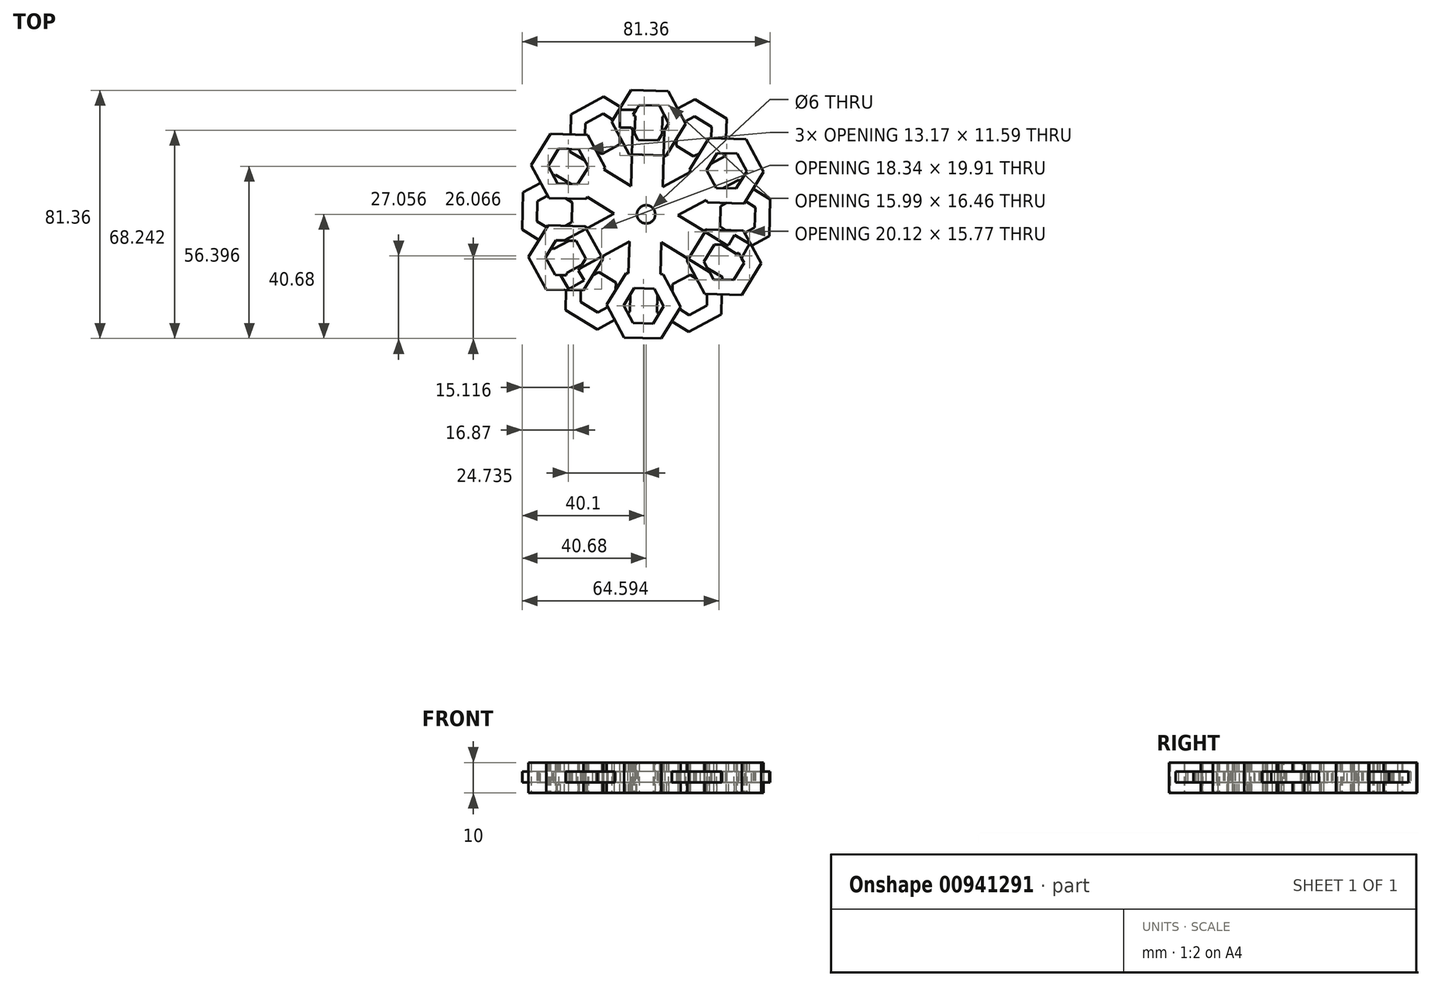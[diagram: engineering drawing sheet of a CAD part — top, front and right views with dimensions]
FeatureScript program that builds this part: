
annotation { "Feature Type Name" : "Feature", "Feature Type Description" : "" }
export const myFeature = defineFeature(function(context is Context, id is Id, definition is map)
    precondition{}
    {
        {
            var Q0;
            Q0=qCreatedBy(makeId("Top.planeOp"),FACE);
            var sketch = newSketch(context, id + "F0", { "sketchPlane" : qUnion([Q0])});
            skCircle(sketch, "E0", {"center": v(0, 0) * mm, "radius": 3 * mm});
            skSolve(sketch);
        }
        {
            var Q0;
            Q0=qCreatedBy(makeId("Top.planeOp"),FACE);
            var sketch = newSketch(context, id + "F1", { "sketchPlane" : qUnion([Q0])});
            skPoint(sketch, "E1.0.midPoint", {"position": v(0, 0) * mm});
            skCircle(sketch, "E2.cCircle", {"center": v(0, 0) * mm, "radius": 9.08 * mm, "construction": true});
            skLineSegment(sketch, "E2.0", {"start": v(-8.93, 5.5) * mm, "end": v(0.29, 10.48) * mm});
            skLineSegment(sketch, "E2.1", {"start": v(0.29, 10.48) * mm, "end": v(9.22, 5) * mm});
            skLineSegment(sketch, "E2.2", {"start": v(9.22, 5) * mm, "end": v(8.93, -5.5) * mm});
            skLineSegment(sketch, "E2.3", {"start": v(8.93, -5.5) * mm, "end": v(-0.29, -10.48) * mm});
            skLineSegment(sketch, "E2.4", {"start": v(-0.29, -10.48) * mm, "end": v(-9.22, -5) * mm});
            skLineSegment(sketch, "E2.5", {"start": v(-9.22, -5) * mm, "end": v(-8.93, 5.5) * mm});
            skPoint(sketch, "E2.0.midPoint", {"position": v(-4.32, 7.99) * mm});
            skLineSegment(sketch, "E3", {"start": v(-9.22, -5) * mm, "end": v(-30, -4.42) * mm});
            skLineSegment(sketch, "E4", {"start": v(-8.93, 5.5) * mm, "end": v(-30, 6.07) * mm});
            skLineSegment(sketch, "E5", {"start": v(-30, 6.07) * mm, "end": v(-30, -4.42) * mm});
            skCircle(sketch, "E6.cCircle", {"center": v(-30, 0.83) * mm, "radius": 10.52 * mm, "construction": true});
            skLineSegment(sketch, "E6.0", {"start": v(-40.68, -4.95) * mm, "end": v(-40.35, 7.2) * mm});
            skLineSegment(sketch, "E6.1", {"start": v(-40.35, 7.2) * mm, "end": v(-29.66, 12.98) * mm});
            skLineSegment(sketch, "E6.2", {"start": v(-29.66, 12.98) * mm, "end": v(-19.3, 6.61) * mm});
            skLineSegment(sketch, "E6.3", {"start": v(-19.3, 6.61) * mm, "end": v(-19.64, -5.54) * mm});
            skLineSegment(sketch, "E6.4", {"start": v(-19.64, -5.54) * mm, "end": v(-30.33, -11.32) * mm});
            skLineSegment(sketch, "E6.5", {"start": v(-30.33, -11.32) * mm, "end": v(-40.68, -4.95) * mm});
            skPoint(sketch, "E6.0.midPoint", {"position": v(-40.52, 1.12) * mm});
            skLineSegment(sketch, "E7.0", {"start": v(-35.8, -2.3) * mm, "end": v(-35.6, 4.28) * mm});
            skLineSegment(sketch, "E7.1", {"start": v(-35.6, 4.28) * mm, "end": v(-29.81, 7.41) * mm});
            skLineSegment(sketch, "E7.2", {"start": v(-29.81, 7.41) * mm, "end": v(-24.2, 3.96) * mm});
            skLineSegment(sketch, "E7.3", {"start": v(-24.2, 3.96) * mm, "end": v(-24.38, -2.62) * mm});
            skLineSegment(sketch, "E7.4", {"start": v(-24.38, -2.62) * mm, "end": v(-30.18, -5.76) * mm});
            skLineSegment(sketch, "E7.5", {"start": v(-30.18, -5.76) * mm, "end": v(-35.8, -2.3) * mm});
            skPoint(sketch, "E7.0.midPoint", {"position": v(-35.7, 0.99) * mm});
            skLineSegment(sketch, "E8.1.1", {"start": v(-15.38, -13.42) * mm, "end": v(-5.03, -19.78) * mm});
            skLineSegment(sketch, "E8.1.2", {"start": v(-5.36, -31.93) * mm, "end": v(-16.05, -37.71) * mm});
            skLineSegment(sketch, "E8.1.3", {"start": v(-16.05, -37.71) * mm, "end": v(-26.4, -31.35) * mm});
            skLineSegment(sketch, "E8.1.4", {"start": v(-26.4, -31.35) * mm, "end": v(-26.07, -19.2) * mm});
            skLineSegment(sketch, "E8.1.5", {"start": v(-26.07, -19.2) * mm, "end": v(-15.38, -13.42) * mm});
            skCircle(sketch, "E8.1.6", {"center": v(-15.72, -25.56) * mm, "radius": 9.53 * mm, "construction": true});
            skCircle(sketch, "E8.1.7", {"center": v(-15.72, -25.56) * mm, "radius": 10.52 * mm, "construction": true});
            skLineSegment(sketch, "E8.1.8", {"start": v(-5.03, -19.78) * mm, "end": v(-5.36, -31.93) * mm});
            skLineSegment(sketch, "E8.1.9", {"start": v(-9.22, -5) * mm, "end": v(-20.26, -22.94) * mm});
            skLineSegment(sketch, "E8.1.10", {"start": v(-0.29, -10.48) * mm, "end": v(-11.17, -28.19) * mm});
            skLineSegment(sketch, "E8.1.11", {"start": v(-20.26, -22.94) * mm, "end": v(-11.17, -28.19) * mm});
            skLineSegment(sketch, "E8.2.1", {"start": v(3.93, -20.03) * mm, "end": v(14.62, -14.24) * mm});
            skLineSegment(sketch, "E8.2.2", {"start": v(24.97, -20.6) * mm, "end": v(24.63, -32.76) * mm});
            skLineSegment(sketch, "E8.2.3", {"start": v(24.63, -32.76) * mm, "end": v(13.95, -38.54) * mm});
            skLineSegment(sketch, "E8.2.4", {"start": v(13.95, -38.54) * mm, "end": v(3.6, -32.18) * mm});
            skLineSegment(sketch, "E8.2.5", {"start": v(3.6, -32.18) * mm, "end": v(3.93, -20.03) * mm});
            skCircle(sketch, "E8.2.6", {"center": v(14.28, -26.4) * mm, "radius": 9.53 * mm, "construction": true});
            skCircle(sketch, "E8.2.7", {"center": v(14.28, -26.4) * mm, "radius": 10.52 * mm, "construction": true});
            skLineSegment(sketch, "E8.2.8", {"start": v(14.62, -14.24) * mm, "end": v(24.97, -20.6) * mm});
            skLineSegment(sketch, "E8.2.9", {"start": v(-0.29, -10.48) * mm, "end": v(9.74, -29.01) * mm});
            skLineSegment(sketch, "E8.2.10", {"start": v(8.93, -5.5) * mm, "end": v(18.82, -23.77) * mm});
            skLineSegment(sketch, "E8.2.11", {"start": v(9.74, -29.01) * mm, "end": v(18.82, -23.77) * mm});
            skLineSegment(sketch, "E8.3.1", {"start": v(19.3, -6.61) * mm, "end": v(19.64, 5.54) * mm});
            skLineSegment(sketch, "E8.3.2", {"start": v(30.33, 11.32) * mm, "end": v(40.68, 4.95) * mm});
            skLineSegment(sketch, "E8.3.3", {"start": v(40.68, 4.95) * mm, "end": v(40.35, -7.2) * mm});
            skLineSegment(sketch, "E8.3.4", {"start": v(40.35, -7.2) * mm, "end": v(29.66, -12.98) * mm});
            skLineSegment(sketch, "E8.3.5", {"start": v(29.66, -12.98) * mm, "end": v(19.3, -6.61) * mm});
            skCircle(sketch, "E8.3.6", {"center": v(30, -0.83) * mm, "radius": 9.53 * mm, "construction": true});
            skCircle(sketch, "E8.3.7", {"center": v(30, -0.83) * mm, "radius": 10.52 * mm, "construction": true});
            skLineSegment(sketch, "E8.3.8", {"start": v(19.64, 5.54) * mm, "end": v(30.33, 11.32) * mm});
            skLineSegment(sketch, "E8.3.9", {"start": v(8.93, -5.5) * mm, "end": v(30, -6.07) * mm});
            skLineSegment(sketch, "E8.3.10", {"start": v(9.22, 5) * mm, "end": v(30, 4.42) * mm});
            skLineSegment(sketch, "E8.3.11", {"start": v(30, -6.07) * mm, "end": v(30, 4.42) * mm});
            skLineSegment(sketch, "E8.4.1", {"start": v(15.38, 13.42) * mm, "end": v(5.03, 19.78) * mm});
            skLineSegment(sketch, "E8.4.2", {"start": v(5.36, 31.93) * mm, "end": v(16.05, 37.71) * mm});
            skLineSegment(sketch, "E8.4.3", {"start": v(16.05, 37.71) * mm, "end": v(26.4, 31.35) * mm});
            skLineSegment(sketch, "E8.4.4", {"start": v(26.4, 31.35) * mm, "end": v(26.07, 19.2) * mm});
            skLineSegment(sketch, "E8.4.5", {"start": v(26.07, 19.2) * mm, "end": v(15.38, 13.42) * mm});
            skCircle(sketch, "E8.4.6", {"center": v(15.72, 25.56) * mm, "radius": 9.53 * mm, "construction": true});
            skCircle(sketch, "E8.4.7", {"center": v(15.72, 25.56) * mm, "radius": 10.52 * mm, "construction": true});
            skLineSegment(sketch, "E8.4.8", {"start": v(5.03, 19.78) * mm, "end": v(5.36, 31.93) * mm});
            skLineSegment(sketch, "E8.4.9", {"start": v(9.22, 5) * mm, "end": v(20.26, 22.94) * mm});
            skLineSegment(sketch, "E8.4.10", {"start": v(0.29, 10.48) * mm, "end": v(11.17, 28.19) * mm});
            skLineSegment(sketch, "E8.4.11", {"start": v(20.26, 22.94) * mm, "end": v(11.17, 28.19) * mm});
            skLineSegment(sketch, "E8.5.1", {"start": v(-3.93, 20.03) * mm, "end": v(-14.62, 14.24) * mm});
            skLineSegment(sketch, "E8.5.2", {"start": v(-24.97, 20.6) * mm, "end": v(-24.63, 32.76) * mm});
            skLineSegment(sketch, "E8.5.3", {"start": v(-24.63, 32.76) * mm, "end": v(-13.95, 38.54) * mm});
            skLineSegment(sketch, "E8.5.4", {"start": v(-13.95, 38.54) * mm, "end": v(-3.6, 32.18) * mm});
            skLineSegment(sketch, "E8.5.5", {"start": v(-3.6, 32.18) * mm, "end": v(-3.93, 20.03) * mm});
            skCircle(sketch, "E8.5.6", {"center": v(-14.28, 26.4) * mm, "radius": 9.53 * mm, "construction": true});
            skCircle(sketch, "E8.5.7", {"center": v(-14.28, 26.4) * mm, "radius": 10.52 * mm, "construction": true});
            skLineSegment(sketch, "E8.5.8", {"start": v(-14.62, 14.24) * mm, "end": v(-24.97, 20.6) * mm});
            skLineSegment(sketch, "E8.5.9", {"start": v(0.29, 10.48) * mm, "end": v(-9.74, 29.01) * mm});
            skLineSegment(sketch, "E8.5.10", {"start": v(-8.93, 5.5) * mm, "end": v(-18.82, 23.77) * mm});
            skLineSegment(sketch, "E8.5.11", {"start": v(-9.74, 29.01) * mm, "end": v(-18.82, 23.77) * mm});
            skLineSegment(sketch, "E9.1.1", {"start": v(8.67, -22.94) * mm, "end": v(14.46, -19.8) * mm});
            skPoint(sketch, "E9.1.2", {"position": v(17, -31.41) * mm});
            skCircle(sketch, "E9.1.3", {"center": v(14.28, -26.4) * mm, "radius": 5.7 * mm, "construction": true});
            skLineSegment(sketch, "E9.2.1", {"start": v(15.53, 18.98) * mm, "end": v(9.92, 22.43) * mm});
            skPoint(sketch, "E9.2.2", {"position": v(18.7, 30.42) * mm});
            skCircle(sketch, "E9.2.3", {"center": v(15.72, 25.56) * mm, "radius": 5.7 * mm, "construction": true});
            skLineSegment(sketch, "E10.1.1", {"start": v(-15.53, -18.98) * mm, "end": v(-9.92, -22.43) * mm});
            skLineSegment(sketch, "E10.1.2", {"start": v(-9.92, -22.43) * mm, "end": v(-10.1, -29.01) * mm});
            skLineSegment(sketch, "E10.1.3", {"start": v(-10.1, -29.01) * mm, "end": v(-15.9, -32.15) * mm});
            skLineSegment(sketch, "E10.1.4", {"start": v(-15.9, -32.15) * mm, "end": v(-21.51, -28.7) * mm});
            skLineSegment(sketch, "E10.1.5", {"start": v(-21.51, -28.7) * mm, "end": v(-21.33, -22.11) * mm});
            skLineSegment(sketch, "E10.1.6", {"start": v(-21.33, -22.11) * mm, "end": v(-15.53, -18.98) * mm});
            skLineSegment(sketch, "E10.2.2", {"start": v(14.46, -19.8) * mm, "end": v(20.08, -23.26) * mm});
            skLineSegment(sketch, "E10.2.3", {"start": v(20.08, -23.26) * mm, "end": v(19.9, -29.84) * mm});
            skLineSegment(sketch, "E10.2.4", {"start": v(19.9, -29.84) * mm, "end": v(14.1, -32.98) * mm});
            skLineSegment(sketch, "E10.2.5", {"start": v(14.1, -32.98) * mm, "end": v(8.49, -29.53) * mm});
            skLineSegment(sketch, "E10.2.6", {"start": v(8.49, -29.53) * mm, "end": v(8.67, -22.94) * mm});
            skLineSegment(sketch, "E10.3.1", {"start": v(24.2, -3.96) * mm, "end": v(24.38, 2.62) * mm});
            skLineSegment(sketch, "E10.3.2", {"start": v(24.38, 2.62) * mm, "end": v(30.18, 5.76) * mm});
            skLineSegment(sketch, "E10.3.3", {"start": v(30.18, 5.76) * mm, "end": v(35.8, 2.3) * mm});
            skLineSegment(sketch, "E10.3.4", {"start": v(35.8, 2.3) * mm, "end": v(35.6, -4.28) * mm});
            skLineSegment(sketch, "E10.3.5", {"start": v(35.6, -4.28) * mm, "end": v(29.81, -7.41) * mm});
            skLineSegment(sketch, "E10.3.6", {"start": v(29.81, -7.41) * mm, "end": v(24.2, -3.96) * mm});
            skLineSegment(sketch, "E10.4.2", {"start": v(9.92, 22.43) * mm, "end": v(10.1, 29.01) * mm});
            skLineSegment(sketch, "E10.4.3", {"start": v(10.1, 29.01) * mm, "end": v(15.9, 32.15) * mm});
            skLineSegment(sketch, "E10.4.4", {"start": v(15.9, 32.15) * mm, "end": v(21.51, 28.7) * mm});
            skLineSegment(sketch, "E10.4.5", {"start": v(21.51, 28.7) * mm, "end": v(21.33, 22.11) * mm});
            skLineSegment(sketch, "E10.4.6", {"start": v(21.33, 22.11) * mm, "end": v(15.53, 18.98) * mm});
            skLineSegment(sketch, "E10.5.1", {"start": v(-8.67, 22.94) * mm, "end": v(-14.46, 19.8) * mm});
            skLineSegment(sketch, "E10.5.2", {"start": v(-14.46, 19.8) * mm, "end": v(-20.08, 23.26) * mm});
            skLineSegment(sketch, "E10.5.3", {"start": v(-20.08, 23.26) * mm, "end": v(-19.9, 29.84) * mm});
            skLineSegment(sketch, "E10.5.4", {"start": v(-19.9, 29.84) * mm, "end": v(-14.1, 32.98) * mm});
            skLineSegment(sketch, "E10.5.5", {"start": v(-14.1, 32.98) * mm, "end": v(-8.49, 29.53) * mm});
            skLineSegment(sketch, "E10.5.6", {"start": v(-8.49, 29.53) * mm, "end": v(-8.67, 22.94) * mm});
            skLineSegment(sketch, "E11", {"start": v(-15.38, -13.42) * mm, "end": v(-7.57, -13.42) * mm});
            skLineSegment(sketch, "E12", {"start": v(-7.57, -13.42) * mm, "end": v(-5.03, -19.78) * mm});
            skLineSegment(sketch, "E13.1.1", {"start": v(15.4, 0.15) * mm, "end": v(19.64, 5.54) * mm});
            skLineSegment(sketch, "E13.1.3", {"start": v(19.3, -6.61) * mm, "end": v(15.4, 0.15) * mm});
            skLineSegment(sketch, "E13.2.1", {"start": v(-7.83, 13.27) * mm, "end": v(-14.62, 14.24) * mm});
            skLineSegment(sketch, "E13.2.3", {"start": v(-3.93, 20.03) * mm, "end": v(-7.83, 13.27) * mm});
            skLineSegment(sketch, "E14.bottom", {"start": v(28.48, 8.57) * mm, "end": v(34.28, 8.57) * mm});
            skLineSegment(sketch, "E14.top", {"start": v(28.48, -10.48) * mm, "end": v(34.28, -10.48) * mm});
            skLineSegment(sketch, "E14.left", {"start": v(28.48, 8.57) * mm, "end": v(28.48, -10.48) * mm});
            skLineSegment(sketch, "E14.right", {"start": v(34.28, 8.57) * mm, "end": v(34.28, -10.48) * mm});
            skLineSegment(sketch, "E15.1.1", {"start": v(-21.66, 20.37) * mm, "end": v(-5.17, 29.9) * mm});
            skLineSegment(sketch, "E15.1.2", {"start": v(-21.66, 20.37) * mm, "end": v(-24.57, 25.4) * mm});
            skLineSegment(sketch, "E15.1.3", {"start": v(-24.57, 25.4) * mm, "end": v(-8.07, 34.93) * mm});
            skLineSegment(sketch, "E15.1.4", {"start": v(-5.17, 29.9) * mm, "end": v(-8.07, 34.93) * mm});
            skLineSegment(sketch, "E15.2.1", {"start": v(-6.81, -28.95) * mm, "end": v(-23.31, -19.42) * mm});
            skLineSegment(sketch, "E15.2.2", {"start": v(-6.81, -28.95) * mm, "end": v(-9.71, -33.98) * mm});
            skLineSegment(sketch, "E15.2.3", {"start": v(-9.71, -33.98) * mm, "end": v(-26.21, -24.45) * mm});
            skLineSegment(sketch, "E15.2.4", {"start": v(-23.31, -19.42) * mm, "end": v(-26.21, -24.45) * mm});
            skSolve(sketch);
        }
        {
            var Q0;
            Q0 = qSketchRegion(id + "F1", true);
            extrude(context, id + "F2", {"entities" : qUnion([Q0]), "depth" : 3.5 * mm, "offsetDistance" : 25.4 * mm});
        }
        {
            var Q0;
            Q0=makeQuery(id+"F0.imprint","IMPRINT",FACE,{"disambiguationData":[TD([[makeQuery(id+"F0.imprint","IMPRINT",EDGE,{"derivedFrom":sQuery(id+"F0.wireOp",EDGE,"E0")}),1.0]])]});
            extrude(context, id + "F3", {"entities" : qUnion([Q0]), "operationType" : NewBodyOperationType.REMOVE, "oppositeDirection" : true, "depth" : 25.4 * mm, "offsetDistance" : 25.4 * mm, "hasSecondDirection" : true, "secondDirectionOppositeDirection" : false, "secondDirectionDepth" : 25.4 * mm});
        }
        {
            var Q0;
            Q0=makeQuery(id+"F2.opExtrude","SWEPT_BODY",BODY,{"disambiguationData":[OSD([sQuery(id+"F1.wireOp",EDGE,"E3"),sQuery(id+"F1.wireOp",EDGE,"E4"),sQuery(id+"F1.wireOp",EDGE,"E6.0"),sQuery(id+"F1.wireOp",EDGE,"E6.1"),sQuery(id+"F1.wireOp",EDGE,"E6.2"),sQuery(id+"F1.wireOp",EDGE,"E6.3"),sQuery(id+"F1.wireOp",EDGE,"E6.4"),sQuery(id+"F1.wireOp",EDGE,"E6.5"),sQuery(id+"F1.wireOp",EDGE,"E7.0"),sQuery(id+"F1.wireOp",EDGE,"E7.1"),sQuery(id+"F1.wireOp",EDGE,"E7.2"),sQuery(id+"F1.wireOp",EDGE,"E7.3"),sQuery(id+"F1.wireOp",EDGE,"E7.4"),sQuery(id+"F1.wireOp",EDGE,"E7.5"),sQuery(id+"F1.wireOp",EDGE,"E8.1.1"),sQuery(id+"F1.wireOp",EDGE,"E8.1.2"),sQuery(id+"F1.wireOp",EDGE,"E8.1.3"),sQuery(id+"F1.wireOp",EDGE,"E8.1.4"),sQuery(id+"F1.wireOp",EDGE,"E8.1.5"),sQuery(id+"F1.wireOp",EDGE,"E8.1.8"),sQuery(id+"F1.wireOp",EDGE,"E8.1.9"),sQuery(id+"F1.wireOp",EDGE,"E8.1.10"),sQuery(id+"F1.wireOp",EDGE,"E8.2.1"),sQuery(id+"F1.wireOp",EDGE,"E8.2.2"),sQuery(id+"F1.wireOp",EDGE,"E8.2.3"),sQuery(id+"F1.wireOp",EDGE,"E8.2.4"),sQuery(id+"F1.wireOp",EDGE,"E8.2.5"),sQuery(id+"F1.wireOp",EDGE,"E8.2.8"),sQuery(id+"F1.wireOp",EDGE,"E8.2.9"),sQuery(id+"F1.wireOp",EDGE,"E8.2.10"),sQuery(id+"F1.wireOp",EDGE,"E8.3.1"),sQuery(id+"F1.wireOp",EDGE,"E8.3.2"),sQuery(id+"F1.wireOp",EDGE,"E8.3.3"),sQuery(id+"F1.wireOp",EDGE,"E8.3.4"),sQuery(id+"F1.wireOp",EDGE,"E8.3.5"),sQuery(id+"F1.wireOp",EDGE,"E8.3.8"),sQuery(id+"F1.wireOp",EDGE,"E8.3.9"),sQuery(id+"F1.wireOp",EDGE,"E8.3.10"),sQuery(id+"F1.wireOp",EDGE,"E8.4.1"),sQuery(id+"F1.wireOp",EDGE,"E8.4.2"),sQuery(id+"F1.wireOp",EDGE,"E8.4.3"),sQuery(id+"F1.wireOp",EDGE,"E8.4.4"),sQuery(id+"F1.wireOp",EDGE,"E8.4.5"),sQuery(id+"F1.wireOp",EDGE,"E8.4.8"),sQuery(id+"F1.wireOp",EDGE,"E8.4.9"),sQuery(id+"F1.wireOp",EDGE,"E8.4.10"),sQuery(id+"F1.wireOp",EDGE,"E8.5.1"),sQuery(id+"F1.wireOp",EDGE,"E8.5.2"),sQuery(id+"F1.wireOp",EDGE,"E8.5.3"),sQuery(id+"F1.wireOp",EDGE,"E8.5.4"),sQuery(id+"F1.wireOp",EDGE,"E8.5.5"),sQuery(id+"F1.wireOp",EDGE,"E8.5.8"),sQuery(id+"F1.wireOp",EDGE,"E8.5.9"),sQuery(id+"F1.wireOp",EDGE,"E8.5.10")])]});
            var Q1;
            Q1=makeQuery(id+"F3.boolean.opBoolean","INTERSECT",EDGE,{"derivedFrom":[makeQuery(id+"F2.opExtrude","CAP_FACE",FACE,{"disambiguationData":[OSD([sQuery(id+"F1.wireOp",EDGE,"E3"),sQuery(id+"F1.wireOp",EDGE,"E4"),sQuery(id+"F1.wireOp",EDGE,"E6.0"),sQuery(id+"F1.wireOp",EDGE,"E6.1"),sQuery(id+"F1.wireOp",EDGE,"E6.2"),sQuery(id+"F1.wireOp",EDGE,"E6.3"),sQuery(id+"F1.wireOp",EDGE,"E6.4"),sQuery(id+"F1.wireOp",EDGE,"E6.5"),sQuery(id+"F1.wireOp",EDGE,"E7.0"),sQuery(id+"F1.wireOp",EDGE,"E7.1"),sQuery(id+"F1.wireOp",EDGE,"E7.2"),sQuery(id+"F1.wireOp",EDGE,"E7.3"),sQuery(id+"F1.wireOp",EDGE,"E7.4"),sQuery(id+"F1.wireOp",EDGE,"E7.5"),sQuery(id+"F1.wireOp",EDGE,"E8.1.1"),sQuery(id+"F1.wireOp",EDGE,"E8.1.2"),sQuery(id+"F1.wireOp",EDGE,"E8.1.3"),sQuery(id+"F1.wireOp",EDGE,"E8.1.4"),sQuery(id+"F1.wireOp",EDGE,"E8.1.5"),sQuery(id+"F1.wireOp",EDGE,"E8.1.8"),sQuery(id+"F1.wireOp",EDGE,"E8.1.9"),sQuery(id+"F1.wireOp",EDGE,"E8.1.10"),sQuery(id+"F1.wireOp",EDGE,"E8.2.1"),sQuery(id+"F1.wireOp",EDGE,"E8.2.2"),sQuery(id+"F1.wireOp",EDGE,"E8.2.3"),sQuery(id+"F1.wireOp",EDGE,"E8.2.4"),sQuery(id+"F1.wireOp",EDGE,"E8.2.5"),sQuery(id+"F1.wireOp",EDGE,"E8.2.8"),sQuery(id+"F1.wireOp",EDGE,"E8.2.9"),sQuery(id+"F1.wireOp",EDGE,"E8.2.10"),sQuery(id+"F1.wireOp",EDGE,"E8.3.1"),sQuery(id+"F1.wireOp",EDGE,"E8.3.2"),sQuery(id+"F1.wireOp",EDGE,"E8.3.3"),sQuery(id+"F1.wireOp",EDGE,"E8.3.4"),sQuery(id+"F1.wireOp",EDGE,"E8.3.5"),sQuery(id+"F1.wireOp",EDGE,"E8.3.8"),sQuery(id+"F1.wireOp",EDGE,"E8.3.9"),sQuery(id+"F1.wireOp",EDGE,"E8.3.10"),sQuery(id+"F1.wireOp",EDGE,"E8.4.1"),sQuery(id+"F1.wireOp",EDGE,"E8.4.2"),sQuery(id+"F1.wireOp",EDGE,"E8.4.3"),sQuery(id+"F1.wireOp",EDGE,"E8.4.4"),sQuery(id+"F1.wireOp",EDGE,"E8.4.5"),sQuery(id+"F1.wireOp",EDGE,"E8.4.8"),sQuery(id+"F1.wireOp",EDGE,"E8.4.9"),sQuery(id+"F1.wireOp",EDGE,"E8.4.10"),sQuery(id+"F1.wireOp",EDGE,"E8.5.1"),sQuery(id+"F1.wireOp",EDGE,"E8.5.2"),sQuery(id+"F1.wireOp",EDGE,"E8.5.3"),sQuery(id+"F1.wireOp",EDGE,"E8.5.4"),sQuery(id+"F1.wireOp",EDGE,"E8.5.5"),sQuery(id+"F1.wireOp",EDGE,"E8.5.8"),sQuery(id+"F1.wireOp",EDGE,"E8.5.9"),sQuery(id+"F1.wireOp",EDGE,"E8.5.10")])],"isStart":false}),makeQuery(id+"F3.opExtrude","SWEPT_FACE",FACE,{"disambiguationData":[OSD([sQuery(id+"F0.wireOp",EDGE,"E0")])]})]});
            circularPattern(context, id + "F4", {"entities" : qUnion([Q0]), "axis" : qUnion([Q1]), "angle" : 360 * degree, "instanceCount" : 4, "equalSpace" : true});
        }
        {
            var Q0;
            Q0=makeQuery(id+"F4.opPattern","COPY",FACE,{"derivedFrom":makeQuery(id+"F2.opExtrude","CAP_FACE",FACE,{"disambiguationData":[OSD([sQuery(id+"F1.wireOp",EDGE,"E3"),sQuery(id+"F1.wireOp",EDGE,"E4"),sQuery(id+"F1.wireOp",EDGE,"E6.0"),sQuery(id+"F1.wireOp",EDGE,"E6.1"),sQuery(id+"F1.wireOp",EDGE,"E6.2"),sQuery(id+"F1.wireOp",EDGE,"E6.3"),sQuery(id+"F1.wireOp",EDGE,"E6.4"),sQuery(id+"F1.wireOp",EDGE,"E6.5"),sQuery(id+"F1.wireOp",EDGE,"E7.0"),sQuery(id+"F1.wireOp",EDGE,"E7.1"),sQuery(id+"F1.wireOp",EDGE,"E7.2"),sQuery(id+"F1.wireOp",EDGE,"E7.3"),sQuery(id+"F1.wireOp",EDGE,"E7.4"),sQuery(id+"F1.wireOp",EDGE,"E7.5"),sQuery(id+"F1.wireOp",EDGE,"E8.1.1"),sQuery(id+"F1.wireOp",EDGE,"E8.1.2"),sQuery(id+"F1.wireOp",EDGE,"E8.1.3"),sQuery(id+"F1.wireOp",EDGE,"E8.1.4"),sQuery(id+"F1.wireOp",EDGE,"E8.1.5"),sQuery(id+"F1.wireOp",EDGE,"E8.1.8"),sQuery(id+"F1.wireOp",EDGE,"E8.1.9"),sQuery(id+"F1.wireOp",EDGE,"E8.1.10"),sQuery(id+"F1.wireOp",EDGE,"E8.2.1"),sQuery(id+"F1.wireOp",EDGE,"E8.2.2"),sQuery(id+"F1.wireOp",EDGE,"E8.2.3"),sQuery(id+"F1.wireOp",EDGE,"E8.2.4"),sQuery(id+"F1.wireOp",EDGE,"E8.2.5"),sQuery(id+"F1.wireOp",EDGE,"E8.2.8"),sQuery(id+"F1.wireOp",EDGE,"E8.2.9"),sQuery(id+"F1.wireOp",EDGE,"E8.2.10"),sQuery(id+"F1.wireOp",EDGE,"E8.3.1"),sQuery(id+"F1.wireOp",EDGE,"E8.3.2"),sQuery(id+"F1.wireOp",EDGE,"E8.3.3"),sQuery(id+"F1.wireOp",EDGE,"E8.3.4"),sQuery(id+"F1.wireOp",EDGE,"E8.3.5"),sQuery(id+"F1.wireOp",EDGE,"E8.3.8"),sQuery(id+"F1.wireOp",EDGE,"E8.3.9"),sQuery(id+"F1.wireOp",EDGE,"E8.3.10"),sQuery(id+"F1.wireOp",EDGE,"E8.4.1"),sQuery(id+"F1.wireOp",EDGE,"E8.4.2"),sQuery(id+"F1.wireOp",EDGE,"E8.4.3"),sQuery(id+"F1.wireOp",EDGE,"E8.4.4"),sQuery(id+"F1.wireOp",EDGE,"E8.4.5"),sQuery(id+"F1.wireOp",EDGE,"E8.4.8"),sQuery(id+"F1.wireOp",EDGE,"E8.4.9"),sQuery(id+"F1.wireOp",EDGE,"E8.4.10"),sQuery(id+"F1.wireOp",EDGE,"E8.5.1"),sQuery(id+"F1.wireOp",EDGE,"E8.5.2"),sQuery(id+"F1.wireOp",EDGE,"E8.5.3"),sQuery(id+"F1.wireOp",EDGE,"E8.5.4"),sQuery(id+"F1.wireOp",EDGE,"E8.5.5"),sQuery(id+"F1.wireOp",EDGE,"E8.5.8"),sQuery(id+"F1.wireOp",EDGE,"E8.5.9"),sQuery(id+"F1.wireOp",EDGE,"E8.5.10")])],"isStart":false}),"instanceName":"1"});
            extrude(context, id + "F5", {"entities" : qUnion([Q0]), "operationType" : NewBodyOperationType.ADD, "oppositeDirection" : true, "depth" : 7 * mm, "offsetDistance" : 25.4 * mm, "hasSecondDirection" : true, "secondDirectionOppositeDirection" : false, "secondDirectionDepth" : 3 * mm});
        }
    });
